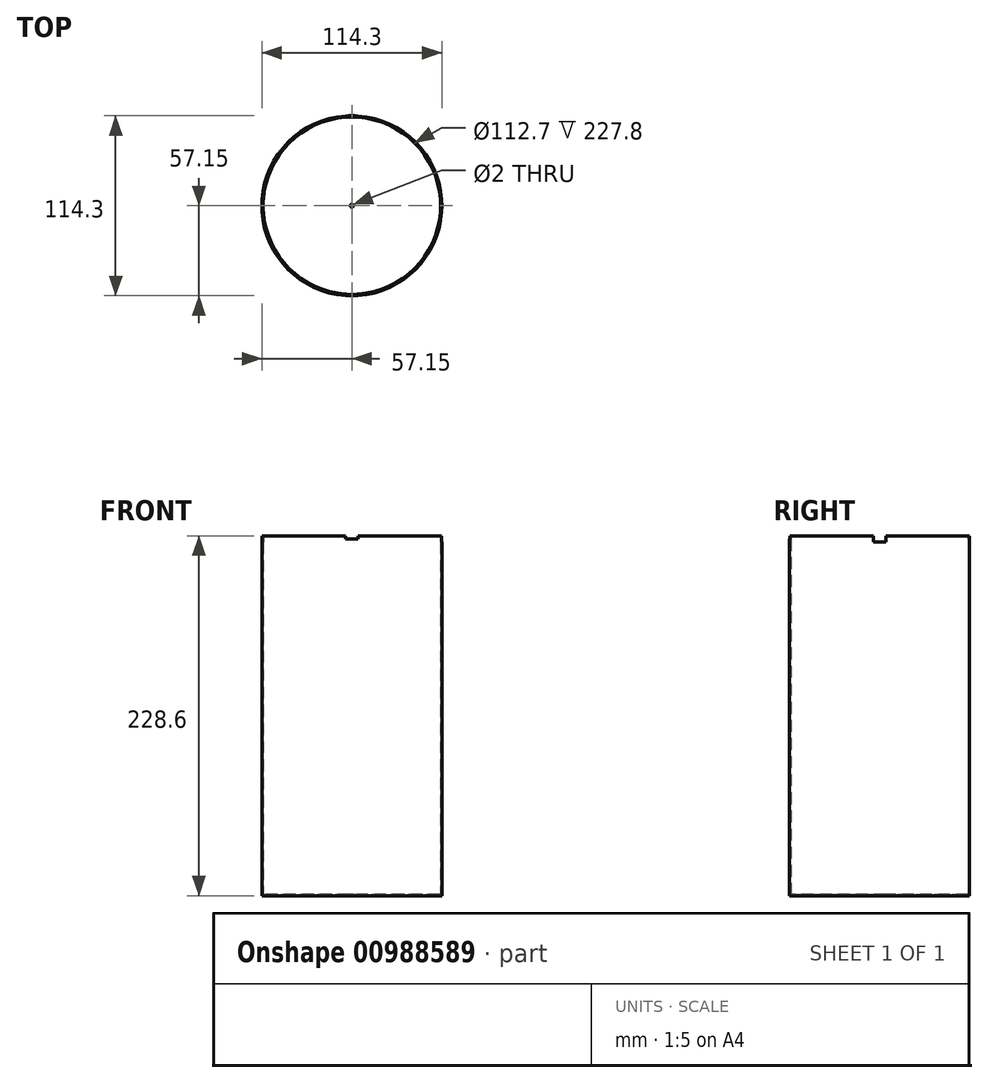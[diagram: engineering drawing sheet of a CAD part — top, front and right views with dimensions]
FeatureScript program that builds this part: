
annotation { "Feature Type Name" : "Feature", "Feature Type Description" : "" }
export const myFeature = defineFeature(function(context is Context, id is Id, definition is map)
    precondition{}
    {
        {
            var Q0;
            Q0=qCreatedBy(makeId("Top.planeOp"),FACE);
            var sketch = newSketch(context, id + "F0", { "sketchPlane" : qUnion([Q0])});
            skCircle(sketch, "E0", {"center": v(0, 0) * mm, "radius": 57.15 * mm});
            skSolve(sketch);
        }
        {
            var Q0;
            Q0=makeQuery(id+"F0.imprint","IMPRINT",FACE,{"disambiguationData":[TD([[makeQuery(id+"F0.imprint","IMPRINT",EDGE,{"derivedFrom":sQuery(id+"F0.wireOp",EDGE,"E0")}),1.0]])]});
            extrude(context, id + "F1", {"entities" : qUnion([Q0]), "depth" : 228.6 * mm, "offsetDistance" : 25.4 * mm});
        }
        {
            var Q0;
            Q0=makeQuery(id+"F1.opExtrude","CAP_FACE",FACE,{"disambiguationData":[OSD([sQuery(id+"F0.wireOp",EDGE,"E0")])],"isStart":false});
            shell(context, id + "F2", {"entities" : qUnion([Q0]), "thickness" : 0.8 * mm});
        }
        {
            var Q0;
            {var subQ0=sQuery(id+"F0.wireOp",EDGE,"E0");Q0=makeQuery(id+"F2.opShell","OFFSET_FACE",FACE,{"disambiguationData":[OSD([subQ0]),TDD([makeQuery(id+"F1.opExtrude","CAP_FACE",FACE,{"disambiguationData":[OSD([subQ0])],"isStart":true})])]});}
            var sketch = newSketch(context, id + "F3", { "sketchPlane" : qUnion([Q0])});
            skCircle(sketch, "E1", {"center": v(0, 0) * mm, "radius": 1 * mm});
            skSolve(sketch);
        }
        {
            var Q0;
            Q0=qSketchRegion(id+"F3",true);
            extrude(context, id + "F4", {"entities" : qUnion([Q0]), "operationType" : NewBodyOperationType.REMOVE, "endBound" : BoundingType.UP_TO_NEXT, "oppositeDirection" : true, "depth" : 25.4 * mm, "offsetDistance" : 25.4 * mm});
        }
        {
            var Q0;
            Q0=qCreatedBy(makeId("Front.planeOp"),FACE);
            var sketch = newSketch(context, id + "F5", { "sketchPlane" : qUnion([Q0])});
            skLineSegment(sketch, "E2", {"start": v(-4, 228.6) * mm, "end": v(4, 228.6) * mm});
            skLineSegment(sketch, "E3", {"start": v(-4, 228.6) * mm, "end": v(-4, 226.6) * mm});
            skLineSegment(sketch, "E4", {"start": v(4, 228.6) * mm, "end": v(4, 226.6) * mm});
            skLineSegment(sketch, "E5", {"start": v(4, 226.6) * mm, "end": v(-4, 226.6) * mm});
            skLineSegment(sketch, "E6", {"start": v(0, 228.6) * mm, "end": v(0, 226.6) * mm, "construction": true});
            skSolve(sketch);
        }
        {
            var Q0;
            Q0 = qSketchRegion(id + "F5", true);
            extrude(context, id + "F6", {"entities" : qUnion([Q0]), "operationType" : NewBodyOperationType.REMOVE, "endBound" : BoundingType.THROUGH_ALL, "oppositeDirection" : true, "depth" : 25.4 * mm, "offsetDistance" : 25.4 * mm, "hasSecondDirection" : true, "secondDirectionBound" : SecondDirectionBoundingType.THROUGH_ALL, "secondDirectionOppositeDirection" : false, "secondDirectionDepth" : 25.4 * mm});
        }
        {
            var Q0;
            Q0=qCreatedBy(makeId("Right.planeOp"),FACE);
            var sketch = newSketch(context, id + "F7", { "sketchPlane" : qUnion([Q0])});
            skLineSegment(sketch, "E7", {"start": v(-4, 228.6) * mm, "end": v(4, 228.6) * mm});
            skLineSegment(sketch, "E8", {"start": v(-4, 228.6) * mm, "end": v(-4, 224.6) * mm});
            skLineSegment(sketch, "E9", {"start": v(4, 228.6) * mm, "end": v(4, 224.6) * mm});
            skLineSegment(sketch, "E10", {"start": v(4, 224.6) * mm, "end": v(-4, 224.6) * mm});
            skSolve(sketch);
        }
        {
            var Q0;
            Q0 = qSketchRegion(id + "F7", true);
            extrude(context, id + "F8", {"entities" : qUnion([Q0]), "operationType" : NewBodyOperationType.REMOVE, "endBound" : BoundingType.THROUGH_ALL, "oppositeDirection" : true, "depth" : 25.4 * mm, "offsetDistance" : 25.4 * mm, "hasSecondDirection" : true, "secondDirectionBound" : SecondDirectionBoundingType.THROUGH_ALL, "secondDirectionOppositeDirection" : false, "secondDirectionDepth" : 25.4 * mm});
        }
    });
